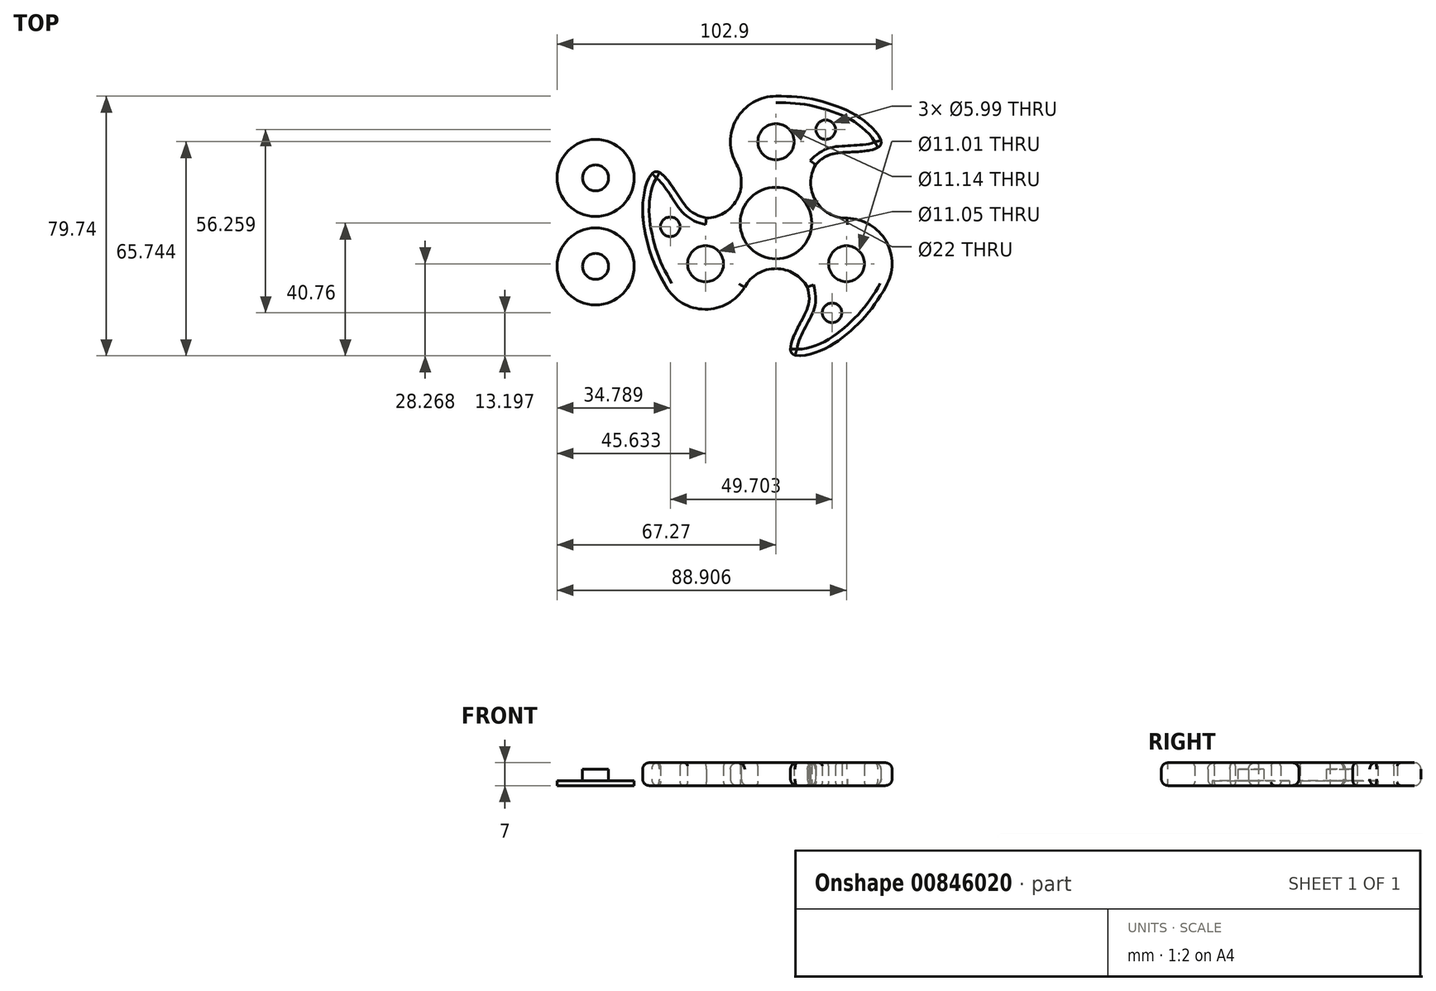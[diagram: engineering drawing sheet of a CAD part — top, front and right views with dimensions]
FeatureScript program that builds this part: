
annotation { "Feature Type Name" : "Feature", "Feature Type Description" : "" }
export const myFeature = defineFeature(function(context is Context, id is Id, definition is map)
    precondition{}
    {
        {
            var Q0;
            Q0=qCreatedBy(makeId("Top.planeOp"),FACE);
            var sketch = newSketch(context, id + "F0", { "sketchPlane" : qUnion([Q0])});
            skCircle(sketch, "E0", {"center": v(0, 0) * mm, "radius": 11 * mm});
            skArc(sketch, "E1", {"start": v(-9.64, -19.7) * mm, "mid": v(0, -14) * mm, "end": v(9.64, -19.7) * mm});
            skArc(sketch, "E2", {"start": v(21.88, 1.5) * mm, "mid": v(12.2, 6.87) * mm, "end": v(12.1, 17.95) * mm});
            skFitSpline(sketch, "E3", {"points": [v(0, 38.98) * mm, v(14.82, 37.12) * mm, v(26.3, 31.99) * mm, v(32.13, 24.04) * mm, v(21.46, 21.72) * mm, v(12.1, 17.95) * mm], "startDerivative": vector(103.34, -0.06) * mm, "endDerivative": vector(-52.51, -53.48) * mm});
            skArc(sketch, "E4", {"start": v(0, 38.98) * mm, "mid": v(-12.13, 31.96) * mm, "end": v(-12.1, 17.94) * mm});
            skFitSpline(sketch, "E5.MirrorCS", {"points": [v(-33.77, -19.46) * mm, v(-39.56, -5.72) * mm, v(-40.85, 6.78) * mm, v(-36.88, 15.81) * mm, v(-29.54, 7.73) * mm, v(-21.4, 1.5) * mm], "startDerivative": vector(-51.6, 89.54) * mm, "endDerivative": vector(72.56, -18.75) * mm});
            skFitSpline(sketch, "E6.MirrorCS", {"points": [v(33.75, -19.5) * mm, v(24.73, -31.4) * mm, v(14.55, -38.77) * mm, v(4.75, -39.85) * mm, v(8.08, -29.45) * mm, v(9.64, -19.7) * mm], "startDerivative": vector(-51.73, -89.46) * mm, "endDerivative": vector(-20.05, 72.22) * mm});
            skArc(sketch, "E7", {"start": v(33.75, -19.5) * mm, "mid": v(33.82, -5.6) * mm, "end": v(21.88, 1.5) * mm});
            skArc(sketch, "E8", {"start": v(-33.77, -19.46) * mm, "mid": v(-21.78, -26.48) * mm, "end": v(-9.64, -19.7) * mm});
            skArc(sketch, "E9", {"start": v(-21.4, 1.5) * mm, "mid": v(-12.08, 7.07) * mm, "end": v(-12.1, 17.94) * mm});
            skCircle(sketch, "E10", {"center": v(15.26, 28.7) * mm, "radius": 3 * mm});
            skCircle(sketch, "E11", {"center": v(-21.64, -12.5) * mm, "radius": 5.53 * mm});
            skCircle(sketch, "E12", {"center": v(0, 24.98) * mm, "radius": 5.57 * mm});
            skCircle(sketch, "E13", {"center": v(21.64, -12.5) * mm, "radius": 5.5 * mm});
            skCircle(sketch, "E14.MirrorC", {"center": v(-32.48, -1.13) * mm, "radius": 3 * mm});
            skCircle(sketch, "E15.MirrorC", {"center": v(17.22, -27.56) * mm, "radius": 3 * mm});
            skSolve(sketch);
        }
        {
            var Q0;
            Q0=makeQuery(id+"F0.imprint","IMPRINT",FACE,{"disambiguationData":[TD([[makeQuery(id+"F0.imprint","IMPRINT",EDGE,{"derivedFrom":sQuery(id+"F0.wireOp",EDGE,"E0")}),-1.0]])]});
            extrude(context, id + "F1", {"entities" : qUnion([Q0]), "depth" : 7 * mm, "offsetDistance" : 25 * mm});
        }
        {
            var Q0;
            Q0=makeQuery(id+"F1.opExtrude","CAP_EDGE",EDGE,{"disambiguationData":[OSD([sQuery(id+"F0.wireOp",EDGE,"E9")])],"isStart":false});
            var Q1;
            Q1=makeQuery(id+"F1.opExtrude","CAP_EDGE",EDGE,{"disambiguationData":[OSD([sQuery(id+"F0.wireOp",EDGE,"E2")])],"isStart":false});
            var Q2;
            Q2=makeQuery(id+"F1.opExtrude","CAP_EDGE",EDGE,{"disambiguationData":[OSD([sQuery(id+"F0.wireOp",EDGE,"E1")])],"isStart":false});
            fillet(context, id + "F2", {"entities" : qUnion([Q0, Q1, Q2]), "radius" : 2 * mm, "tangentPropagation" : true, "allowEdgeOverflow" : false});
        }
        {
            var Q0;
            Q0=makeQuery(id+"F1.opExtrude","CAP_EDGE",EDGE,{"disambiguationData":[OSD([sQuery(id+"F0.wireOp",EDGE,"E3")])],"isStart":false});
            var Q1;
            Q1=makeQuery(id+"F1.opExtrude","CAP_EDGE",EDGE,{"disambiguationData":[OSD([sQuery(id+"F0.wireOp",EDGE,"E5.MirrorCS")])],"isStart":false});
            var Q2;
            Q2=makeQuery(id+"F1.opExtrude","CAP_EDGE",EDGE,{"disambiguationData":[OSD([sQuery(id+"F0.wireOp",EDGE,"E6.MirrorCS"),sQuery(id+"F0.wireOp",EDGE,"E6.MirrorCS")])],"isStart":false});
            var Q3;
            Q3=makeQuery(id+"F1.opExtrude","CAP_EDGE",EDGE,{"disambiguationData":[OSD([sQuery(id+"F0.wireOp",EDGE,"E7")])],"isStart":false});
            var Q4;
            Q4=makeQuery(id+"F1.opExtrude","CAP_EDGE",EDGE,{"disambiguationData":[OSD([sQuery(id+"F0.wireOp",EDGE,"E8")])],"isStart":false});
            var Q5;
            Q5=makeQuery(id+"F1.opExtrude","CAP_EDGE",EDGE,{"disambiguationData":[OSD([sQuery(id+"F0.wireOp",EDGE,"E4")])],"isStart":false});
            fillet(context, id + "F3", {"entities" : qUnion([Q0, Q1, Q2, Q3, Q4, Q5]), "radius" : 2 * mm, "tangentPropagation" : true, "allowEdgeOverflow" : false});
        }
        {
            var Q0;
            Q0=makeQuery(id+"F1.opExtrude","CAP_EDGE",EDGE,{"disambiguationData":[OSD([sQuery(id+"F0.wireOp",EDGE,"E1")])],"isStart":true});
            var Q1;
            Q1=makeQuery(id+"F1.opExtrude","CAP_EDGE",EDGE,{"disambiguationData":[OSD([sQuery(id+"F0.wireOp",EDGE,"E2")])],"isStart":true});
            var Q2;
            Q2=makeQuery(id+"F1.opExtrude","CAP_EDGE",EDGE,{"disambiguationData":[OSD([sQuery(id+"F0.wireOp",EDGE,"E9")])],"isStart":true});
            var Q3;
            Q3=makeQuery(id+"F1.opExtrude","CAP_EDGE",EDGE,{"disambiguationData":[OSD([sQuery(id+"F0.wireOp",EDGE,"E3")])],"isStart":true});
            var Q4;
            Q4=makeQuery(id+"F1.opExtrude","CAP_EDGE",EDGE,{"disambiguationData":[OSD([sQuery(id+"F0.wireOp",EDGE,"E4")])],"isStart":true});
            var Q5;
            Q5=makeQuery(id+"F1.opExtrude","CAP_EDGE",EDGE,{"disambiguationData":[OSD([sQuery(id+"F0.wireOp",EDGE,"E5.MirrorCS")])],"isStart":true});
            var Q6;
            Q6=makeQuery(id+"F1.opExtrude","CAP_EDGE",EDGE,{"disambiguationData":[OSD([sQuery(id+"F0.wireOp",EDGE,"E8")])],"isStart":true});
            var Q7;
            Q7=makeQuery(id+"F1.opExtrude","CAP_EDGE",EDGE,{"disambiguationData":[OSD([sQuery(id+"F0.wireOp",EDGE,"E6.MirrorCS"),sQuery(id+"F0.wireOp",EDGE,"E6.MirrorCS")])],"isStart":true});
            var Q8;
            Q8=makeQuery(id+"F1.opExtrude","CAP_EDGE",EDGE,{"disambiguationData":[OSD([sQuery(id+"F0.wireOp",EDGE,"E7")])],"isStart":true});
            fillet(context, id + "F4", {"entities" : qUnion([Q0, Q1, Q2, Q3, Q4, Q5, Q6, Q7, Q8]), "radius" : 2 * mm, "tangentPropagation" : true, "allowEdgeOverflow" : false});
        }
        {
            var Q0;
            Q0=makeQuery(id+"F1.opExtrude","CAP_EDGE",EDGE,{"disambiguationData":[OSD([sQuery(id+"F0.wireOp",EDGE,"E12")])],"isStart":false});
            var Q1;
            Q1=makeQuery(id+"F1.opExtrude","CAP_EDGE",EDGE,{"disambiguationData":[OSD([sQuery(id+"F0.wireOp",EDGE,"E10")])],"isStart":false});
            var Q2;
            Q2=makeQuery(id+"F1.opExtrude","CAP_EDGE",EDGE,{"disambiguationData":[OSD([sQuery(id+"F0.wireOp",EDGE,"E13")])],"isStart":false});
            var Q3;
            Q3=makeQuery(id+"F1.opExtrude","CAP_EDGE",EDGE,{"disambiguationData":[OSD([sQuery(id+"F0.wireOp",EDGE,"BPGkPH1c-wJ4s-BxUl-H9XK-bEpJPOhnZw0A")])],"isStart":false});
            var Q4;
            Q4=makeQuery(id+"F1.opExtrude","CAP_EDGE",EDGE,{"disambiguationData":[OSD([sQuery(id+"F0.wireOp",EDGE,"E11")])],"isStart":false});
            var Q5;
            Q5=makeQuery(id+"F1.opExtrude","CAP_EDGE",EDGE,{"disambiguationData":[OSD([sQuery(id+"F0.wireOp",EDGE,"o7rR0OST-ZHvJ-2tTx-IXaI-ngszV4EVDEz4")])],"isStart":false});
            var Q6;
            Q6=makeQuery(id+"F1.opExtrude","CAP_EDGE",EDGE,{"disambiguationData":[OSD([sQuery(id+"F0.wireOp",EDGE,"E14.MirrorC")])],"isStart":false});
            var Q7;
            Q7=makeQuery(id+"F1.opExtrude","CAP_EDGE",EDGE,{"disambiguationData":[OSD([sQuery(id+"F0.wireOp",EDGE,"E15.MirrorC")])],"isStart":false});
            var Q8;
            Q8=makeQuery(id+"F1.opExtrude","CAP_EDGE",EDGE,{"disambiguationData":[OSD([sQuery(id+"F0.wireOp",EDGE,"E11")])],"isStart":true});
            var Q9;
            Q9=makeQuery(id+"F1.opExtrude","CAP_EDGE",EDGE,{"disambiguationData":[OSD([sQuery(id+"F0.wireOp",EDGE,"E14.MirrorC")])],"isStart":true});
            var Q10;
            Q10=makeQuery(id+"F1.opExtrude","CAP_EDGE",EDGE,{"disambiguationData":[OSD([sQuery(id+"F0.wireOp",EDGE,"E13")])],"isStart":true});
            var Q11;
            Q11=makeQuery(id+"F1.opExtrude","CAP_EDGE",EDGE,{"disambiguationData":[OSD([sQuery(id+"F0.wireOp",EDGE,"E15.MirrorC")])],"isStart":true});
            var Q12;
            Q12=makeQuery(id+"F1.opExtrude","CAP_EDGE",EDGE,{"disambiguationData":[OSD([sQuery(id+"F0.wireOp",EDGE,"E12")])],"isStart":true});
            var Q13;
            Q13=makeQuery(id+"F1.opExtrude","CAP_EDGE",EDGE,{"disambiguationData":[OSD([sQuery(id+"F0.wireOp",EDGE,"E10")])],"isStart":true});
            fillet(context, id + "F5", {"entities" : qUnion([Q0, Q1, Q2, Q3, Q4, Q5, Q6, Q7, Q8, Q9, Q10, Q11, Q12, Q13]), "radius" : 1 * mm, "tangentPropagation" : true, "allowEdgeOverflow" : false});
        }
        {
            var Q0;
            Q0=makeQuery(id+"F1.opExtrude","CAP_EDGE",EDGE,{"disambiguationData":[OSD([sQuery(id+"F0.wireOp",EDGE,"E0")])],"isStart":false});
            var Q1;
            Q1=makeQuery(id+"F1.opExtrude","CAP_EDGE",EDGE,{"disambiguationData":[OSD([sQuery(id+"F0.wireOp",EDGE,"E0")])],"isStart":true});
            fillet(context, id + "F6", {"entities" : qUnion([Q0, Q1]), "radius" : 0.5 * mm, "tangentPropagation" : true, "allowEdgeOverflow" : false});
        }
        {
            var Q0;
            Q0=qCreatedBy(makeId("Top.planeOp"),FACE);
            var sketch = newSketch(context, id + "F7", { "sketchPlane" : qUnion([Q0])});
            skCircle(sketch, "E16", {"center": v(-55.42, 13.88) * mm, "radius": 11.85 * mm});
            skCircle(sketch, "E17", {"center": v(-55.42, 13.88) * mm, "radius": 4 * mm});
            skCircle(sketch, "E18", {"center": v(-55.42, -13.3) * mm, "radius": 11.85 * mm});
            skCircle(sketch, "E19", {"center": v(-55.42, -13.3) * mm, "radius": 4 * mm});
            skSolve(sketch);
        }
        {
            var Q0;
            Q0=makeQuery(id+"F7.imprint","IMPRINT",FACE,{"disambiguationData":[TD([[makeQuery(id+"F7.imprint","IMPRINT",EDGE,{"derivedFrom":sQuery(id+"F7.wireOp",EDGE,"QbvqnUuG-a8oH-SnHc-a0OA-Zd9yiuwx99br")}),1.0]])]});
            var Q1;
            Q1=makeQuery(id+"F7.imprint","IMPRINT",FACE,{"disambiguationData":[TD([[makeQuery(id+"F7.imprint","IMPRINT",EDGE,{"derivedFrom":sQuery(id+"F7.wireOp",EDGE,"725891c2-b97f-48d4-844d-feab697eb66f")}),1.0]])]});
            var Q2;
            Q2=makeQuery(id+"F7.imprint","IMPRINT",FACE,{"disambiguationData":[TD([[makeQuery(id+"F7.imprint","IMPRINT",EDGE,{"derivedFrom":sQuery(id+"F7.wireOp",EDGE,"E16")}),1.0]])]});
            var Q3;
            Q3=makeQuery(id+"F7.imprint","IMPRINT",FACE,{"disambiguationData":[TD([[makeQuery(id+"F7.imprint","IMPRINT",EDGE,{"derivedFrom":sQuery(id+"F7.wireOp",EDGE,"E18")}),1.0]])]});
            extrude(context, id + "F8", {"entities" : qUnion([Q0, Q1, Q2, Q3]), "depth" : 1.5 * mm, "offsetDistance" : 25 * mm});
        }
        {
            var Q0;
            Q0=makeQuery(id+"F7.imprint","IMPRINT",FACE,{"disambiguationData":[TD([[makeQuery(id+"F7.imprint","IMPRINT",EDGE,{"derivedFrom":sQuery(id+"F7.wireOp",EDGE,"E17")}),1.0]])]});
            var Q1;
            Q1=makeQuery(id+"F7.imprint","IMPRINT",FACE,{"disambiguationData":[TD([[makeQuery(id+"F7.imprint","IMPRINT",EDGE,{"derivedFrom":sQuery(id+"F7.wireOp",EDGE,"E19")}),1.0]])]});
            extrude(context, id + "F9", {"entities" : qUnion([Q0, Q1]), "operationType" : NewBodyOperationType.ADD, "depth" : 5 * mm, "offsetDistance" : 25 * mm});
        }
    });
